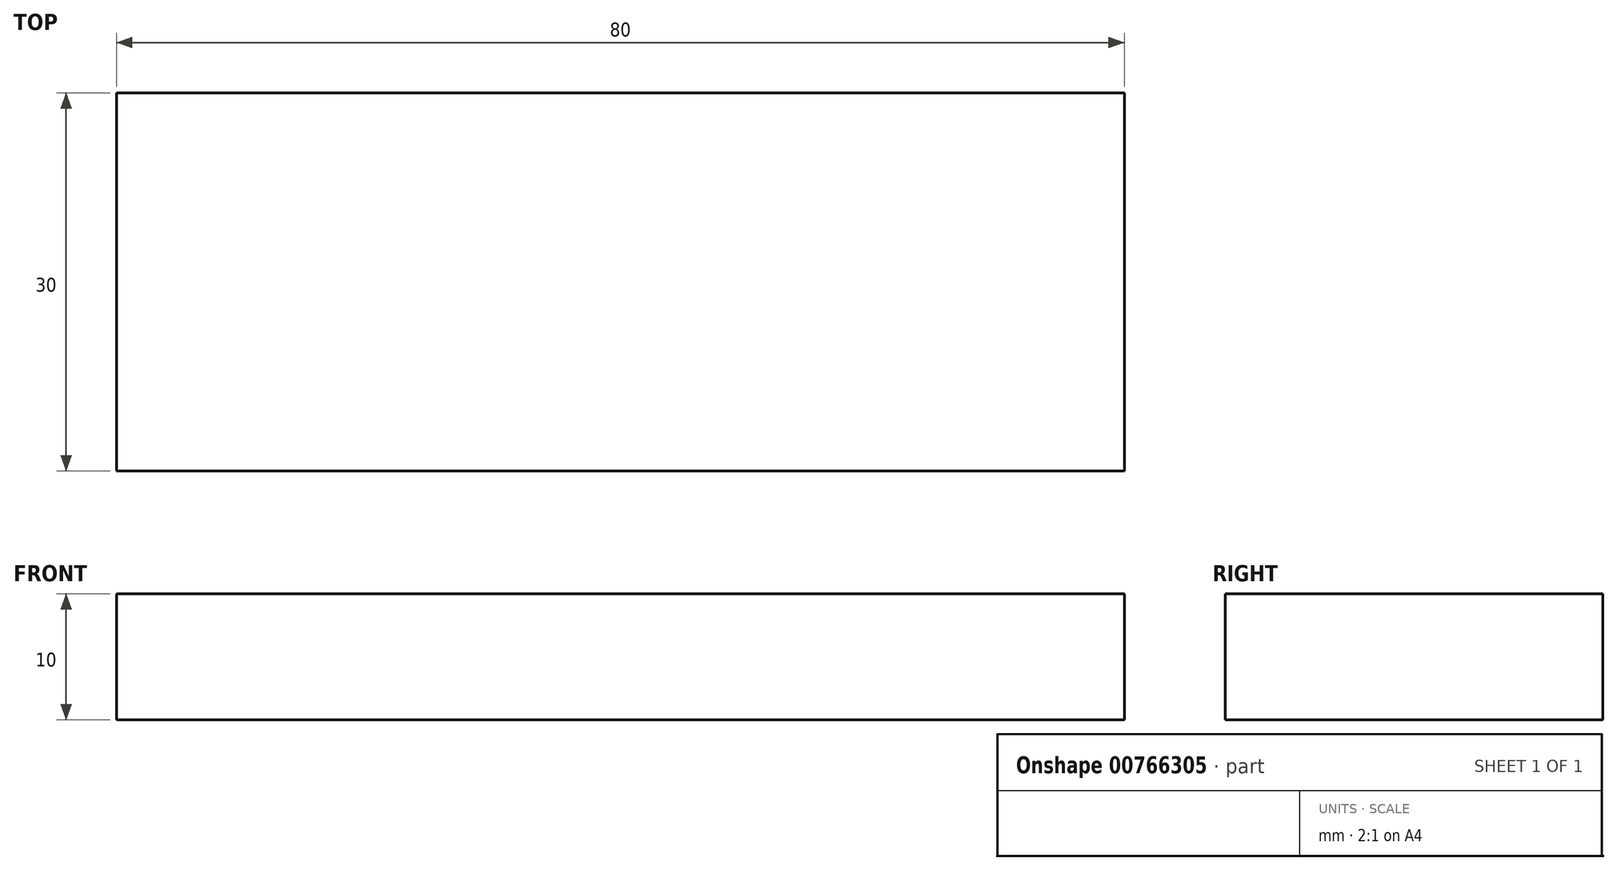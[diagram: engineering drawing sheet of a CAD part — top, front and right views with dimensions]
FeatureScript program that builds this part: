
annotation { "Feature Type Name" : "Feature", "Feature Type Description" : "" }
export const myFeature = defineFeature(function(context is Context, id is Id, definition is map)
    precondition{}
    {
        {
            var Q0;
            Q0=qCreatedBy(makeId("Top.planeOp"),FACE);
            var sketch = newSketch(context, id + "F0", { "sketchPlane" : qUnion([Q0])});
            skLineSegment(sketch, "E0.bottom", {"start": v(40, 15) * mm, "end": v(-40, 15) * mm});
            skLineSegment(sketch, "E0.top", {"start": v(40, -15) * mm, "end": v(-40, -15) * mm});
            skLineSegment(sketch, "E0.left", {"start": v(40, 15) * mm, "end": v(40, -15) * mm});
            skLineSegment(sketch, "E0.right", {"start": v(-40, 15) * mm, "end": v(-40, -15) * mm});
            skPoint(sketch, "E0.middle", {"position": v(0, 0) * mm});
            skSolve(sketch);
        }
        {
            var Q0;
            Q0 = qSketchRegion(id + "F0", true);
            extrude(context, id + "F1", {"entities" : qUnion([Q0]), "depth" : 10 * mm, "offsetDistance" : 25.4 * mm});
        }
    });
